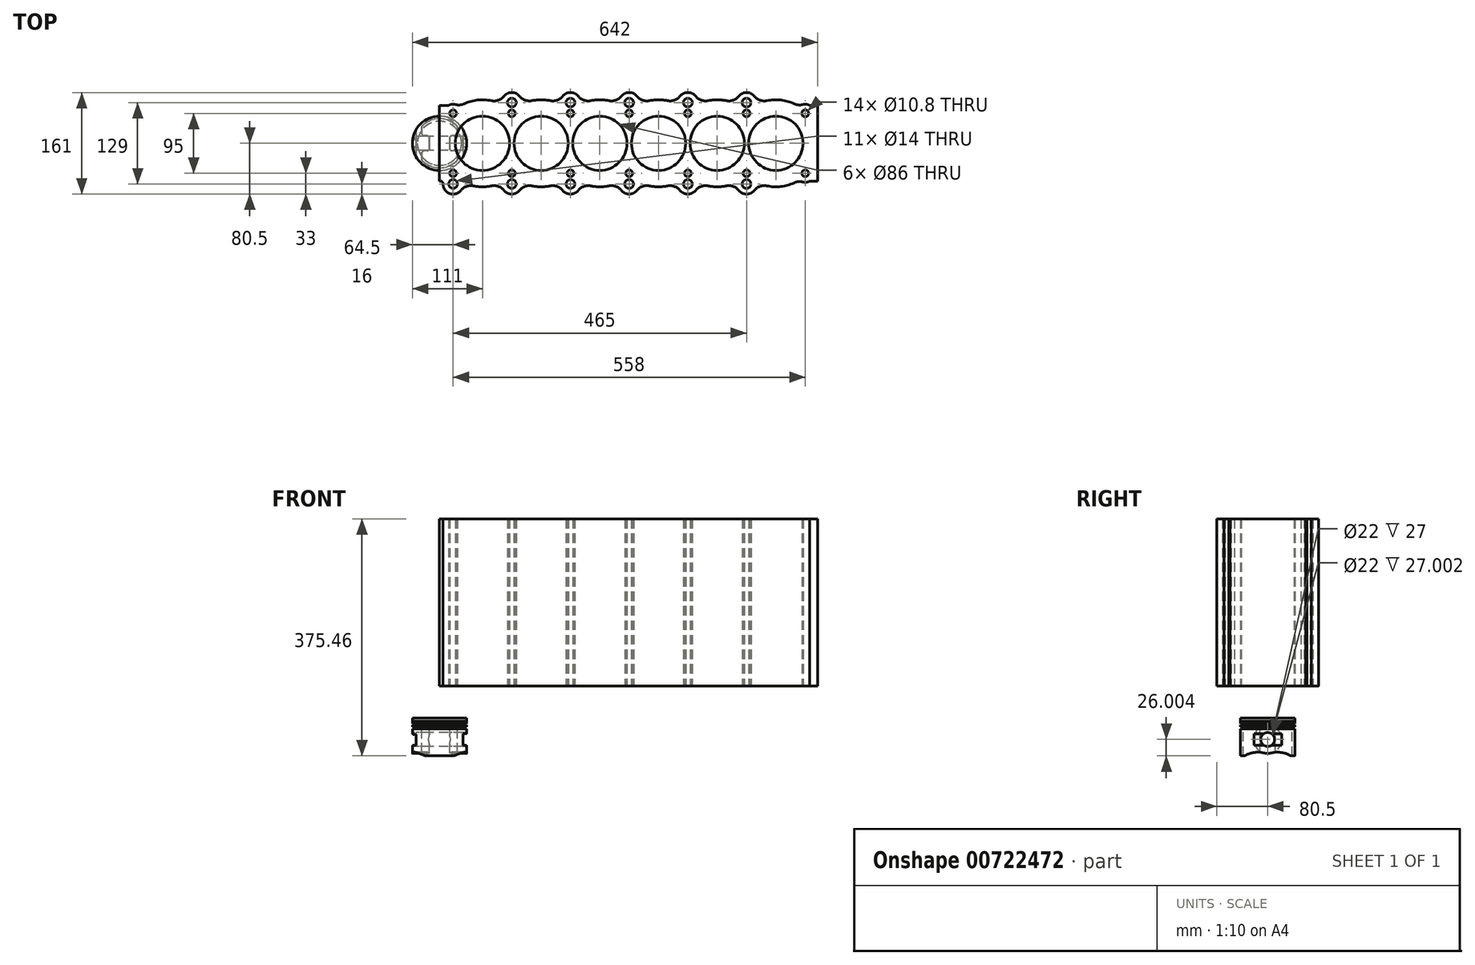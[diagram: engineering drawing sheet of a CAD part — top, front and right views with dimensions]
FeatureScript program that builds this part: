
annotation { "Feature Type Name" : "Feature", "Feature Type Description" : "" }
export const myFeature = defineFeature(function(context is Context, id is Id, definition is map)
    precondition{}
    {
        {
            var Q0;
            Q0=qCreatedBy(makeId("Top.planeOp"),FACE);
            var sketch = newSketch(context, id + "F0", { "sketchPlane" : qUnion([Q0])});
            skCircle(sketch, "E0", {"center": v(68, 0) * mm, "radius": 43 * mm});
            skArc(sketch, "E1", {"start": v(82.3, 67.5) * mm, "mid": v(60.2, 68.56) * mm, "end": v(38.91, 62.57) * mm});
            skCircle(sketch, "E2", {"center": v(114.5, 47.5) * mm, "radius": 5.4 * mm});
            skCircle(sketch, "E3", {"center": v(114.5, 64.5) * mm, "radius": 7 * mm});
            skArc(sketch, "E4", {"start": v(126.97, 74.53) * mm, "mid": v(114.5, 80.5) * mm, "end": v(102.03, 74.53) * mm});
            skCircle(sketch, "E5.1.0.0", {"center": v(161, 0) * mm, "radius": 43 * mm});
            skArc(sketch, "E5.1.0.1", {"start": v(146.7, -67.5) * mm, "mid": v(161, -69) * mm, "end": v(175.3, -67.5) * mm});
            skCircle(sketch, "E5.2.0.0", {"center": v(254, 0) * mm, "radius": 43 * mm});
            skArc(sketch, "E5.2.0.1", {"start": v(239.7, -67.5) * mm, "mid": v(254, -69) * mm, "end": v(268.3, -67.5) * mm});
            skCircle(sketch, "E5.3.0.0", {"center": v(347, 0) * mm, "radius": 43 * mm});
            skArc(sketch, "E5.3.0.1", {"start": v(332.7, -67.5) * mm, "mid": v(347, -69) * mm, "end": v(361.3, -67.5) * mm});
            skCircle(sketch, "E5.4.0.0", {"center": v(440, 0) * mm, "radius": 43 * mm});
            skArc(sketch, "E5.4.0.1", {"start": v(425.7, -67.5) * mm, "mid": v(440, -69) * mm, "end": v(454.3, -67.5) * mm});
            skCircle(sketch, "E5.5.0.0", {"center": v(533, 0) * mm, "radius": 43 * mm});
            skArc(sketch, "E5.5.0.1", {"start": v(518.7, -67.5) * mm, "mid": v(540.8, -68.56) * mm, "end": v(562.09, -62.57) * mm});
            skLineSegment(sketch, "E5.direction1", {"start": v(68, 0) * mm, "end": v(161, 0) * mm, "construction": true});
            skCircle(sketch, "E6.1.0.0", {"center": v(207.5, 47.5) * mm, "radius": 5.4 * mm});
            skCircle(sketch, "E6.1.0.2", {"center": v(207.5, 64.5) * mm, "radius": 7 * mm});
            skCircle(sketch, "E6.2.0.0", {"center": v(300.5, 47.5) * mm, "radius": 5.4 * mm});
            skArc(sketch, "E6.2.0.1", {"start": v(312.97, 74.53) * mm, "mid": v(300.5, 80.5) * mm, "end": v(288.03, 74.53) * mm});
            skCircle(sketch, "E6.2.0.2", {"center": v(300.5, 64.5) * mm, "radius": 7 * mm});
            skCircle(sketch, "E6.3.0.0", {"center": v(393.5, 47.5) * mm, "radius": 5.4 * mm});
            skCircle(sketch, "E6.3.0.2", {"center": v(393.5, 64.5) * mm, "radius": 7 * mm});
            skCircle(sketch, "E6.4.0.0", {"center": v(486.5, 47.5) * mm, "radius": 5.4 * mm});
            skCircle(sketch, "E6.4.0.2", {"center": v(486.5, 64.5) * mm, "radius": 7 * mm});
            skLineSegment(sketch, "E6.direction1", {"start": v(114.5, 47.5) * mm, "end": v(207.5, 47.5) * mm, "construction": true});
            skArc(sketch, "E7.filletArc", {"start": v(126.97, 74.53) * mm, "mid": v(135.84, 68.23) * mm, "end": v(146.7, 67.5) * mm});
            skArc(sketch, "E8.filletArc", {"start": v(82.3, 67.5) * mm, "mid": v(93.16, 68.23) * mm, "end": v(102.03, 74.53) * mm});
            skArc(sketch, "E9.trimOffspring", {"start": v(175.3, 67.5) * mm, "mid": v(161, 69) * mm, "end": v(146.7, 67.5) * mm});
            skArc(sketch, "E10.trimOffspring", {"start": v(219.97, 74.53) * mm, "mid": v(207.5, 80.5) * mm, "end": v(195.03, 74.53) * mm});
            skArc(sketch, "E11.trimOffspring", {"start": v(268.3, 67.5) * mm, "mid": v(254, 69) * mm, "end": v(239.7, 67.5) * mm});
            skArc(sketch, "E12.trimOffspring", {"start": v(361.3, 67.5) * mm, "mid": v(347, 69) * mm, "end": v(332.7, 67.5) * mm});
            skArc(sketch, "E13.trimOffspring", {"start": v(405.97, 74.53) * mm, "mid": v(393.5, 80.5) * mm, "end": v(381.03, 74.53) * mm});
            skArc(sketch, "E14.trimOffspring", {"start": v(454.3, 67.5) * mm, "mid": v(440, 69) * mm, "end": v(425.7, 67.5) * mm});
            skArc(sketch, "E15.trimOffspring", {"start": v(498.97, 74.53) * mm, "mid": v(486.5, 80.5) * mm, "end": v(474.03, 74.53) * mm});
            skArc(sketch, "E16.filletArc", {"start": v(175.3, 67.5) * mm, "mid": v(186.16, 68.23) * mm, "end": v(195.03, 74.53) * mm});
            skArc(sketch, "E17.filletArc", {"start": v(219.97, 74.53) * mm, "mid": v(228.84, 68.23) * mm, "end": v(239.7, 67.5) * mm});
            skArc(sketch, "E18.filletArc", {"start": v(268.3, 67.5) * mm, "mid": v(279.16, 68.23) * mm, "end": v(288.03, 74.53) * mm});
            skArc(sketch, "E19.filletArc", {"start": v(312.97, 74.53) * mm, "mid": v(321.84, 68.23) * mm, "end": v(332.7, 67.5) * mm});
            skArc(sketch, "E20.filletArc", {"start": v(361.3, 67.5) * mm, "mid": v(372.16, 68.23) * mm, "end": v(381.03, 74.53) * mm});
            skArc(sketch, "E21.filletArc", {"start": v(405.97, 74.53) * mm, "mid": v(414.84, 68.23) * mm, "end": v(425.7, 67.5) * mm});
            skArc(sketch, "E22.filletArc", {"start": v(454.3, 67.5) * mm, "mid": v(465.16, 68.23) * mm, "end": v(474.03, 74.53) * mm});
            skArc(sketch, "E23.filletArc", {"start": v(498.97, 74.53) * mm, "mid": v(507.84, 68.23) * mm, "end": v(518.7, 67.5) * mm});
            skLineSegment(sketch, "E24", {"start": v(-32.5, 0) * mm, "end": v(36.17, 0) * mm, "construction": true});
            skArc(sketch, "E25.MirrorCS", {"start": v(82.3, -67.5) * mm, "mid": v(93.16, -68.23) * mm, "end": v(102.03, -74.53) * mm});
            skArc(sketch, "E26.MirrorCS", {"start": v(126.97, -74.53) * mm, "mid": v(114.5, -80.5) * mm, "end": v(102.03, -74.53) * mm});
            skArc(sketch, "E27.MirrorCS", {"start": v(126.97, -74.53) * mm, "mid": v(135.84, -68.23) * mm, "end": v(146.7, -67.5) * mm});
            skArc(sketch, "E28.MirrorCS", {"start": v(175.3, -67.5) * mm, "mid": v(186.16, -68.23) * mm, "end": v(195.03, -74.53) * mm});
            skArc(sketch, "E29.MirrorCS", {"start": v(219.97, -74.53) * mm, "mid": v(207.5, -80.5) * mm, "end": v(195.03, -74.53) * mm});
            skArc(sketch, "E30.MirrorCS", {"start": v(219.97, -74.53) * mm, "mid": v(228.84, -68.23) * mm, "end": v(239.7, -67.5) * mm});
            skArc(sketch, "E31.MirrorCS", {"start": v(268.3, -67.5) * mm, "mid": v(279.16, -68.23) * mm, "end": v(288.03, -74.53) * mm});
            skArc(sketch, "E32.MirrorCS", {"start": v(312.97, -74.53) * mm, "mid": v(300.5, -80.5) * mm, "end": v(288.03, -74.53) * mm});
            skArc(sketch, "E33.MirrorCS", {"start": v(312.97, -74.53) * mm, "mid": v(321.84, -68.23) * mm, "end": v(332.7, -67.5) * mm});
            skArc(sketch, "E34.MirrorCS", {"start": v(361.3, -67.5) * mm, "mid": v(372.16, -68.23) * mm, "end": v(381.03, -74.53) * mm});
            skArc(sketch, "E35.MirrorCS", {"start": v(405.97, -74.53) * mm, "mid": v(393.5, -80.5) * mm, "end": v(381.03, -74.53) * mm});
            skArc(sketch, "E36.MirrorCS", {"start": v(405.97, -74.53) * mm, "mid": v(414.84, -68.23) * mm, "end": v(425.7, -67.5) * mm});
            skArc(sketch, "E37.MirrorCS", {"start": v(454.3, -67.5) * mm, "mid": v(465.16, -68.23) * mm, "end": v(474.03, -74.53) * mm});
            skArc(sketch, "E38.MirrorCS", {"start": v(498.97, -74.53) * mm, "mid": v(486.5, -80.5) * mm, "end": v(474.03, -74.53) * mm});
            skArc(sketch, "E39.MirrorCS", {"start": v(498.97, -74.53) * mm, "mid": v(507.84, -68.23) * mm, "end": v(518.7, -67.5) * mm});
            skCircle(sketch, "E40.MirrorC", {"center": v(114.5, -47.5) * mm, "radius": 5.4 * mm});
            skCircle(sketch, "E41.MirrorC", {"center": v(114.5, -64.5) * mm, "radius": 7 * mm});
            skCircle(sketch, "E42.MirrorC", {"center": v(207.5, -47.5) * mm, "radius": 5.4 * mm});
            skCircle(sketch, "E43.MirrorC", {"center": v(207.5, -64.5) * mm, "radius": 7 * mm});
            skCircle(sketch, "E44.MirrorC", {"center": v(300.5, -47.5) * mm, "radius": 5.4 * mm});
            skCircle(sketch, "E45.MirrorC", {"center": v(300.5, -64.5) * mm, "radius": 7 * mm});
            skCircle(sketch, "E46.MirrorC", {"center": v(393.5, -47.5) * mm, "radius": 5.4 * mm});
            skCircle(sketch, "E47.MirrorC", {"center": v(393.5, -64.5) * mm, "radius": 7 * mm});
            skCircle(sketch, "E48.MirrorC", {"center": v(486.5, -47.5) * mm, "radius": 5.4 * mm});
            skCircle(sketch, "E49.MirrorC", {"center": v(486.5, -64.5) * mm, "radius": 7 * mm});
            skCircle(sketch, "E50", {"center": v(21.5, 47.5) * mm, "radius": 5.4 * mm});
            skArc(sketch, "E51", {"start": v(25.26, 61.4) * mm, "mid": v(19.67, 61.78) * mm, "end": v(14.35, 60) * mm});
            skPoint(sketch, "E52.visualSharp", {"position": v(31.05, 58.27) * mm});
            skArc(sketch, "E52.filletArc", {"start": v(25.26, 61.4) * mm, "mid": v(32.2, 60.78) * mm, "end": v(38.91, 62.57) * mm});
            skLineSegment(sketch, "E53", {"start": v(0, -60) * mm, "end": v(0, 60) * mm});
            skLineSegment(sketch, "E54", {"start": v(0, 60) * mm, "end": v(14.35, 60) * mm});
            skCircle(sketch, "E55", {"center": v(21.5, -64.5) * mm, "radius": 7 * mm});
            skCircle(sketch, "E56", {"center": v(21.5, -47.5) * mm, "radius": 5.4 * mm});
            skArc(sketch, "E57", {"start": v(5.5, -64.1) * mm, "mid": v(16, -79.52) * mm, "end": v(33.97, -74.53) * mm});
            skArc(sketch, "E58.trimOffspring", {"start": v(53.7, -67.5) * mm, "mid": v(68, -69) * mm, "end": v(82.3, -67.5) * mm});
            skLineSegment(sketch, "E59", {"start": v(0, -60) * mm, "end": v(1.5, -60) * mm});
            skPoint(sketch, "E60.visualSharp", {"position": v(37.27, -61.78) * mm});
            skArc(sketch, "E60.filletArc", {"start": v(53.7, -67.5) * mm, "mid": v(42.84, -68.23) * mm, "end": v(33.97, -74.53) * mm});
            skPoint(sketch, "E61.visualSharp", {"position": v(6.15, -60) * mm});
            skArc(sketch, "E61.filletArc", {"start": v(5.5, -64.1) * mm, "mid": v(4.37, -61.2) * mm, "end": v(1.5, -60) * mm});
            skArc(sketch, "E62", {"start": v(586.65, 60) * mm, "mid": v(581.33, 61.78) * mm, "end": v(575.74, 61.4) * mm});
            skLineSegment(sketch, "E63", {"start": v(599, 60) * mm, "end": v(599, -60) * mm});
            skArc(sketch, "E64.trimOffspring", {"start": v(562.09, 62.57) * mm, "mid": v(540.8, 68.56) * mm, "end": v(518.7, 67.5) * mm});
            skPoint(sketch, "E65.visualSharp", {"position": v(569.95, 58.27) * mm});
            skArc(sketch, "E65.filletArc", {"start": v(562.09, 62.57) * mm, "mid": v(568.8, 60.78) * mm, "end": v(575.74, 61.4) * mm});
            skCircle(sketch, "E66", {"center": v(579.5, 47.5) * mm, "radius": 5.4 * mm});
            skLineSegment(sketch, "E67", {"start": v(599, 60) * mm, "end": v(586.65, 60) * mm});
            skCircle(sketch, "E68.MirrorC", {"center": v(579.5, -47.5) * mm, "radius": 5.4 * mm});
            skArc(sketch, "E69.MirrorCS", {"start": v(586.65, -60) * mm, "mid": v(581.33, -61.78) * mm, "end": v(575.74, -61.4) * mm});
            skArc(sketch, "E70.MirrorCS", {"start": v(562.09, -62.57) * mm, "mid": v(568.8, -60.78) * mm, "end": v(575.74, -61.4) * mm});
            skLineSegment(sketch, "E71.MirrorCS", {"start": v(599, -60) * mm, "end": v(586.65, -60) * mm});
            skSolve(sketch);
        }
        {
            var Q0;
            Q0 = qSketchRegion(id + "F0", true);
            extrude(context, id + "F1", {"entities" : qUnion([Q0]), "depth" : 265 * mm, "offsetDistance" : 25 * mm});
        }
        {
            var Q0;
            Q0=qCreatedBy(makeId("Front.planeOp"),FACE);
            var sketch = newSketch(context, id + "F2", { "sketchPlane" : qUnion([Q0])});
            skLineSegment(sketch, "E72", {"start": v(0, 0) * mm, "end": v(0, -114.73) * mm, "construction": true});
            skLineSegment(sketch, "E73", {"start": v(0, -50.46) * mm, "end": v(43, -50.46) * mm});
            skLineSegment(sketch, "E74", {"start": v(43, -50.46) * mm, "end": v(43, -55.46) * mm});
            skLineSegment(sketch, "E75", {"start": v(43, -55.46) * mm, "end": v(35, -55.46) * mm});
            skLineSegment(sketch, "E76", {"start": v(35, -55.46) * mm, "end": v(35, -56.46) * mm});
            skLineSegment(sketch, "E77", {"start": v(35, -56.46) * mm, "end": v(43, -56.46) * mm});
            skLineSegment(sketch, "E78", {"start": v(43, -56.46) * mm, "end": v(43, -59.46) * mm});
            skLineSegment(sketch, "E79", {"start": v(43, -59.46) * mm, "end": v(35, -59.46) * mm});
            skLineSegment(sketch, "E80", {"start": v(35, -59.46) * mm, "end": v(35, -61.46) * mm});
            skLineSegment(sketch, "E81", {"start": v(35, -61.46) * mm, "end": v(43, -61.46) * mm});
            skLineSegment(sketch, "E82", {"start": v(43, -110.46) * mm, "end": v(0, -110.46) * mm});
            skLineSegment(sketch, "E83", {"start": v(43, -61.46) * mm, "end": v(43, -64.46) * mm});
            skLineSegment(sketch, "E84", {"start": v(43, -64.46) * mm, "end": v(35, -64.46) * mm});
            skLineSegment(sketch, "E85", {"start": v(35, -64.46) * mm, "end": v(35, -67.46) * mm});
            skLineSegment(sketch, "E86", {"start": v(35, -67.46) * mm, "end": v(43, -67.46) * mm});
            skLineSegment(sketch, "E87", {"start": v(43, -67.46) * mm, "end": v(43, -110.46) * mm});
            skLineSegment(sketch, "E88", {"start": v(0, -50.46) * mm, "end": v(0, -110.46) * mm});
            skSolve(sketch);
        }
        {
            var Q0;
            Q0=makeQuery(id+"F2.imprint","IMPRINT",FACE,{"disambiguationData":[TD([[makeQuery(id+"F2.imprint","IMPRINT",EDGE,{"derivedFrom":sQuery(id+"F2.wireOp",EDGE,"E73")}),-1.0]])]});
            var Q1;
            Q1=sQuery(id+"F2.wireOp",EDGE,"E72");
            revolve(context, id + "F3", {"surfaceOperationType" : NewSurfaceOperationType.NEW, "entities" : qUnion([Q0]), "axis" : qUnion([Q1]), "revolveType" : RevolveType.FULL});
        }
        {
            var Q0;
            Q0=qCreatedBy(makeId("Right.planeOp"),FACE);
            var sketch = newSketch(context, id + "F4", { "sketchPlane" : qUnion([Q0])});
            skCircle(sketch, "E89", {"center": v(0, -84.46) * mm, "radius": 11 * mm});
            skArc(sketch, "E90", {"start": v(-5.36, -105.91) * mm, "mid": v(0, -106.57) * mm, "end": v(5.36, -105.91) * mm});
            skArc(sketch, "E91", {"start": v(-5.36, -105.91) * mm, "mid": v(-57.2, -149.28) * mm, "end": v(0, -185.3) * mm});
            skArc(sketch, "E92", {"start": v(0, -185.3) * mm, "mid": v(57.2, -149.28) * mm, "end": v(5.36, -105.91) * mm});
            skSolve(sketch);
        }
        {
            var Q0;
            Q0 = qSketchRegion(id + "F4", true);
            extrude(context, id + "F5", {"entities" : qUnion([Q0]), "operationType" : NewBodyOperationType.REMOVE, "endBound" : BoundingType.THROUGH_ALL, "depth" : 54.5 * mm, "offsetDistance" : 25 * mm, "hasSecondDirection" : true, "secondDirectionBound" : SecondDirectionBoundingType.THROUGH_ALL, "secondDirectionOppositeDirection" : true, "secondDirectionDepth" : 25 * mm});
        }
        {
            var Q0;
            Q0=qCreatedBy(makeId("Front.planeOp"),FACE);
            var sketch = newSketch(context, id + "F6", { "sketchPlane" : qUnion([Q0])});
            skLineSegment(sketch, "E93.bottom", {"start": v(43, -75.46) * mm, "end": v(37, -75.46) * mm});
            skLineSegment(sketch, "E93.top", {"start": v(43, -93.46) * mm, "end": v(37, -93.46) * mm});
            skLineSegment(sketch, "E93.left", {"start": v(43, -75.46) * mm, "end": v(43, -93.46) * mm});
            skLineSegment(sketch, "E93.right", {"start": v(37, -75.46) * mm, "end": v(37, -93.46) * mm});
            skLineSegment(sketch, "E94.bottom", {"start": v(-43, -76.52) * mm, "end": v(-37, -76.52) * mm});
            skLineSegment(sketch, "E94.top", {"start": v(-43, -93.96) * mm, "end": v(-37, -93.96) * mm});
            skLineSegment(sketch, "E94.left", {"start": v(-43, -76.52) * mm, "end": v(-43, -93.96) * mm});
            skLineSegment(sketch, "E94.right", {"start": v(-37, -76.52) * mm, "end": v(-37, -93.96) * mm});
            skSolve(sketch);
        }
        {
            var Q0;
            Q0=makeQuery(id+"F6.imprint","IMPRINT",FACE,{"disambiguationData":[TD([[makeQuery(id+"F6.imprint","IMPRINT",EDGE,{"derivedFrom":sQuery(id+"F6.wireOp",EDGE,"E94.bottom")}),-1.0]])]});
            var Q1;
            Q1=makeQuery(id+"F6.imprint","IMPRINT",FACE,{"disambiguationData":[TD([[makeQuery(id+"F6.imprint","IMPRINT",EDGE,{"derivedFrom":sQuery(id+"F6.wireOp",EDGE,"E93.bottom")}),1.0]])]});
            extrude(context, id + "F7", {"entities" : qUnion([Q0, Q1]), "operationType" : NewBodyOperationType.REMOVE, "endBound" : BoundingType.THROUGH_ALL, "oppositeDirection" : true, "depth" : 25 * mm, "offsetDistance" : 25 * mm, "hasSecondDirection" : true, "secondDirectionBound" : SecondDirectionBoundingType.THROUGH_ALL, "secondDirectionOppositeDirection" : false, "secondDirectionDepth" : 25 * mm});
        }
        {
            var Q0;
            Q0=qCreatedBy(makeId("Top.planeOp"),FACE);
            var sketch = newSketch(context, id + "F8", { "sketchPlane" : qUnion([Q0])});
            skArc(sketch, "E95", {"start": v(26.9, 28.23) * mm, "mid": v(0, 39) * mm, "end": v(-26.9, 28.23) * mm});
            skLineSegment(sketch, "E96", {"start": v(-28.15, -25.33) * mm, "end": v(-28.15, -16) * mm});
            skLineSegment(sketch, "E97", {"start": v(-24.15, -12) * mm, "end": v(-20, -12) * mm});
            skLineSegment(sketch, "E98", {"start": v(-16, -8) * mm, "end": v(-16, 8) * mm});
            skLineSegment(sketch, "E99", {"start": v(-20, 12) * mm, "end": v(-24.15, 12) * mm});
            skLineSegment(sketch, "E100", {"start": v(-28.15, 16) * mm, "end": v(-28.15, 25.33) * mm});
            skLineSegment(sketch, "E101", {"start": v(28.15, -25.33) * mm, "end": v(28.15, -16) * mm});
            skLineSegment(sketch, "E102", {"start": v(24.15, -12) * mm, "end": v(20, -12) * mm});
            skLineSegment(sketch, "E103", {"start": v(16, -8) * mm, "end": v(16, 8) * mm});
            skLineSegment(sketch, "E104", {"start": v(20, 12) * mm, "end": v(24.15, 12) * mm});
            skLineSegment(sketch, "E105", {"start": v(28.15, 16) * mm, "end": v(28.15, 25.33) * mm});
            skArc(sketch, "E106.trimOffspring", {"start": v(-26.9, -28.23) * mm, "mid": v(0, -39) * mm, "end": v(26.9, -28.23) * mm});
            skPoint(sketch, "E107.visualSharp", {"position": v(28.15, -12) * mm});
            skArc(sketch, "E107.filletArc", {"start": v(28.15, -16) * mm, "mid": v(26.98, -13.17) * mm, "end": v(24.15, -12) * mm});
            skPoint(sketch, "E108.visualSharp", {"position": v(28.15, -27) * mm});
            skArc(sketch, "E108.filletArc", {"start": v(26.9, -28.23) * mm, "mid": v(27.83, -26.9) * mm, "end": v(28.15, -25.33) * mm});
            skPoint(sketch, "E109.visualSharp", {"position": v(-28.15, -27) * mm});
            skArc(sketch, "E109.filletArc", {"start": v(-28.15, -25.33) * mm, "mid": v(-27.83, -26.9) * mm, "end": v(-26.9, -28.23) * mm});
            skPoint(sketch, "E110.visualSharp", {"position": v(-28.15, -12) * mm});
            skArc(sketch, "E110.filletArc", {"start": v(-24.15, -12) * mm, "mid": v(-26.98, -13.17) * mm, "end": v(-28.15, -16) * mm});
            skPoint(sketch, "E111.visualSharp", {"position": v(16, -12) * mm});
            skArc(sketch, "E111.filletArc", {"start": v(16, -8) * mm, "mid": v(17.17, -10.83) * mm, "end": v(20, -12) * mm});
            skPoint(sketch, "E112.visualSharp", {"position": v(-16, -12) * mm});
            skArc(sketch, "E112.filletArc", {"start": v(-20, -12) * mm, "mid": v(-17.17, -10.83) * mm, "end": v(-16, -8) * mm});
            skPoint(sketch, "E113.visualSharp", {"position": v(16, 12) * mm});
            skArc(sketch, "E113.filletArc", {"start": v(20, 12) * mm, "mid": v(17.17, 10.83) * mm, "end": v(16, 8) * mm});
            skPoint(sketch, "E114.visualSharp", {"position": v(-16, 12) * mm});
            skArc(sketch, "E114.filletArc", {"start": v(-16, 8) * mm, "mid": v(-17.17, 10.83) * mm, "end": v(-20, 12) * mm});
            skPoint(sketch, "E115.visualSharp", {"position": v(28.15, 12) * mm});
            skArc(sketch, "E115.filletArc", {"start": v(24.15, 12) * mm, "mid": v(26.98, 13.17) * mm, "end": v(28.15, 16) * mm});
            skPoint(sketch, "E116.visualSharp", {"position": v(-28.15, 12) * mm});
            skArc(sketch, "E116.filletArc", {"start": v(-28.15, 16) * mm, "mid": v(-26.98, 13.17) * mm, "end": v(-24.15, 12) * mm});
            skPoint(sketch, "E117.visualSharp", {"position": v(-28.15, 27) * mm});
            skArc(sketch, "E117.filletArc", {"start": v(-26.9, 28.23) * mm, "mid": v(-27.83, 26.9) * mm, "end": v(-28.15, 25.33) * mm});
            skPoint(sketch, "E118.visualSharp", {"position": v(28.15, 27) * mm});
            skArc(sketch, "E118.filletArc", {"start": v(28.15, 25.33) * mm, "mid": v(27.83, 26.9) * mm, "end": v(26.9, 28.23) * mm});
            skSolve(sketch);
        }
        {
            var Q0;
            Q0 = qSketchRegion(id + "F8", true);
            extrude(context, id + "F9", {"entities" : qUnion([Q0]), "operationType" : NewBodyOperationType.REMOVE, "oppositeDirection" : true, "depth" : 142 * mm, "offsetDistance" : 25 * mm, "hasSecondDirection" : true, "secondDirectionOppositeDirection" : true, "secondDirectionDepth" : 67 * mm});
        }
        {
            var Q0;
            Q0=makeQuery(id+"F7.boolean.opBoolean","COPY",FACE,{"disambiguationData":[OD(1.0)],"derivedFrom":makeQuery(id+"F7.opExtrude","SWEPT_FACE",FACE,{"disambiguationData":[OSD([sQuery(id+"F6.wireOp",EDGE,"E94.right")])]})});
            var sketch = newSketch(context, id + "F10", { "sketchPlane" : qUnion([Q0])});
            skCircle(sketch, "E119", {"center": v(0, -84.46) * mm, "radius": 11 * mm});
            skSolve(sketch);
        }
        {
            var Q0;
            {var subQ0=sQuery(id+"F10.wireOp",EDGE,"E119");var subQ1=sQuery(id+"F6.wireOp",EDGE,"E94.right");var subQ2=makeQuery(id+"F10.imprint","INTERSECT",VERTEX,{"derivedFrom":[makeQuery(id+"F7.boolean.opBoolean","COPY",EDGE,{"disambiguationData":[OD(1.0)],"derivedFrom":makeQuery(id+"F7.opExtrude","SWEPT_EDGE",EDGE,{"disambiguationData":[OSD([sQuery(id+"F6.wireOp",EDGE,"E94.top"),subQ1])]})}),subQ0]});Q0=makeQuery(id+"F10.imprint","IMPRINT",FACE,{"disambiguationData":[TD([[makeQuery(id+"F10.imprint","IMPRINT",EDGE,{"disambiguationData":[TD([[subQ2,1.0]])],"derivedFrom":subQ0}),1.0]])]});}
            extrude(context, id + "F11", {"entities" : qUnion([Q0]), "oppositeDirection" : true, "depth" : 74 * mm, "offsetDistance" : 25 * mm});
        }
    });
